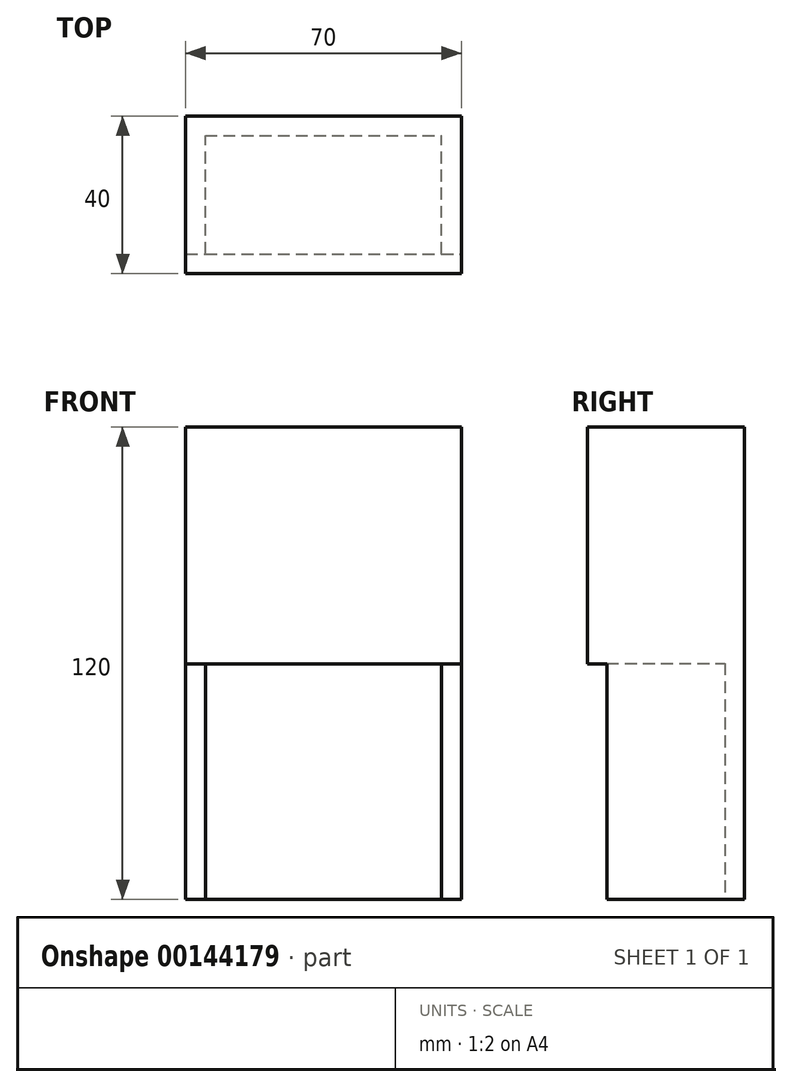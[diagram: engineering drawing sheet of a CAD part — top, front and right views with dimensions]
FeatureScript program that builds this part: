
annotation { "Feature Type Name" : "Feature", "Feature Type Description" : "" }
export const myFeature = defineFeature(function(context is Context, id is Id, definition is map)
    precondition{}
    {
        {
            var Q0;
            Q0=qCreatedBy(makeId("Front.planeOp"),FACE);
            var sketch = newSketch(context, id + "F0", { "sketchPlane" : qUnion([Q0])});
            skLineSegment(sketch, "E0.bottom", {"start": v(-27.57, 0) * mm, "end": v(42.43, 0) * mm});
            skLineSegment(sketch, "E0.top", {"start": v(-27.57, 120) * mm, "end": v(42.43, 120) * mm});
            skLineSegment(sketch, "E0.left", {"start": v(-27.57, 0) * mm, "end": v(-27.57, 120) * mm});
            skLineSegment(sketch, "E0.right", {"start": v(42.43, 0) * mm, "end": v(42.43, 120) * mm});
            skSolve(sketch);
        }
        {
            var Q0;
            Q0 = qSketchRegion(id + "F0", true);
            extrude(context, id + "F1", {"entities" : qUnion([Q0]), "depth" : 40 * mm});
        }
        {
            var Q0;
            Q0=qCreatedBy(makeId("Top.planeOp"),FACE);
            var sketch = newSketch(context, id + "F2", { "sketchPlane" : qUnion([Q0])});
            skLineSegment(sketch, "E1.bottom", {"start": v(-22.57, -35) * mm, "end": v(37.43, -35) * mm});
            skLineSegment(sketch, "E1.top", {"start": v(-22.57, -5) * mm, "end": v(37.43, -5) * mm});
            skLineSegment(sketch, "E1.left", {"start": v(-22.57, -35) * mm, "end": v(-22.57, -5) * mm});
            skLineSegment(sketch, "E1.right", {"start": v(37.43, -35) * mm, "end": v(37.43, -5) * mm});
            skSolve(sketch);
        }
        {
            var Q0;
            Q0 = qSketchRegion(id + "F2", true);
            extrude(context, id + "F3", {"entities" : qUnion([Q0]), "operationType" : NewBodyOperationType.REMOVE, "depth" : 60 * mm});
        }
        {
            var Q0;
            Q0=makeQuery(id+"F1.opExtrude","CAP_FACE",FACE,{"disambiguationData":[OSD([sQuery(id+"F0.wireOp",EDGE,"E0.bottom"),sQuery(id+"F0.wireOp",EDGE,"E0.top"),sQuery(id+"F0.wireOp",EDGE,"E0.left"),sQuery(id+"F0.wireOp",EDGE,"E0.right")])],"isStart":false});
            var sketch = newSketch(context, id + "F4", { "sketchPlane" : qUnion([Q0])});
            skLineSegment(sketch, "E2.bottom", {"start": v(-27.57, 59.78) * mm, "end": v(42.43, 59.78) * mm});
            skLineSegment(sketch, "E2.top", {"start": v(-27.57, 0) * mm, "end": v(42.43, 0) * mm});
            skLineSegment(sketch, "E2.left", {"start": v(-27.57, 59.78) * mm, "end": v(-27.57, 0) * mm});
            skLineSegment(sketch, "E2.right", {"start": v(42.43, 59.78) * mm, "end": v(42.43, 0) * mm});
            skSolve(sketch);
        }
        {
            var Q0;
            Q0=makeQuery(id+"F4.imprint","IMPRINT",FACE,{"disambiguationData":[TD([[makeQuery(id+"F4.imprint","IMPRINT",EDGE,{"derivedFrom":sQuery(id+"F4.wireOp",EDGE,"E2.bottom")}),-1.0]])]});
            extrude(context, id + "F5", {"entities" : qUnion([Q0]), "operationType" : NewBodyOperationType.REMOVE, "oppositeDirection" : true, "depth" : 5 * mm});
        }
    });
